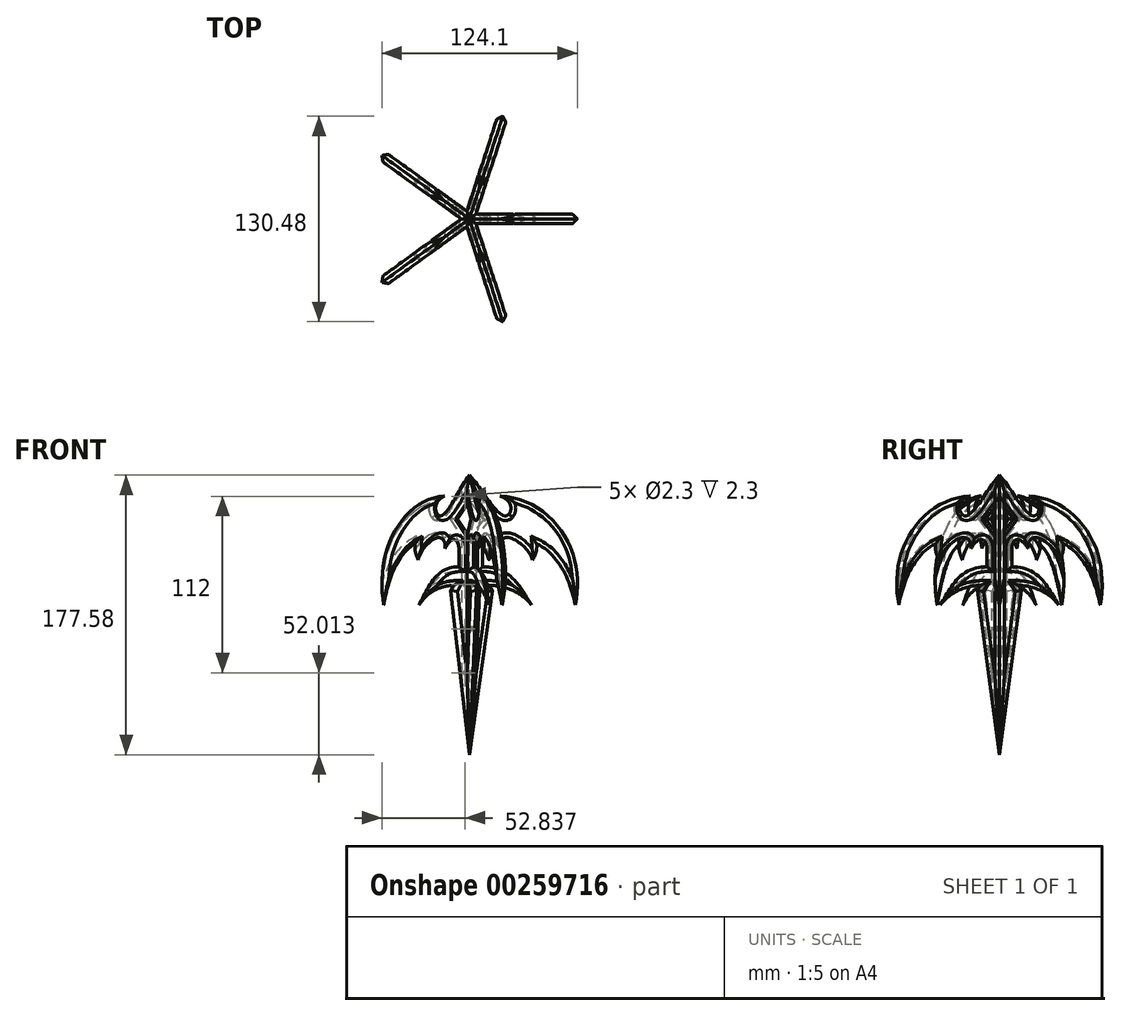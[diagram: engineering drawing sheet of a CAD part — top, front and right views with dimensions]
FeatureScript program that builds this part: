
annotation { "Feature Type Name" : "Feature", "Feature Type Description" : "" }
export const myFeature = defineFeature(function(context is Context, id is Id, definition is map)
    precondition{}
    {
        {
            var Q0;
            Q0=qCreatedBy(makeId("Front.planeOp"),FACE);
            cPlane(context, id + "F0", {"entities" : qUnion([Q0]), "cplaneType" : CPlaneType.OFFSET, "offset" : 3 * mm, "width" : 150 * mm, "height" : 150 * mm});
        }
        {
            var Q0;
            Q0=qCreatedBy(id+"F0.planeOp",FACE);
            var sketch = newSketch(context, id + "F1", { "sketchPlane" : qUnion([Q0])});
            skLineSegment(sketch, "E0", {"start": v(0, 75.85) * mm, "end": v(0, -61.56) * mm, "construction": true});
            skLineSegment(sketch, "E1.MirrorCS", {"start": v(0, 53.4) * mm, "end": v(9.24, 42.07) * mm});
            skLineSegment(sketch, "E2.MirrorCS", {"start": v(9.24, 42.07) * mm, "end": v(0, 30.82) * mm});
            skFitSpline(sketch, "E3.MirrorCS", {"points": [v(25.2, 45.18) * mm, v(0, 70) * mm], "startDerivative": vector(-18.57, -18.17) * mm, "endDerivative": vector(-25.2, 24.83) * mm});
            skFitSpline(sketch, "E4.MirrorCS", {"points": [v(67.26, -12.6) * mm, v(19.54, 56.74) * mm], "startDerivative": vector(23.53, 122.44) * mm, "endDerivative": vector(-82.56, 2.93) * mm});
            skFitSpline(sketch, "E5.MirrorCS", {"points": [v(67.26, -12.6) * mm, v(42.75, 26.42) * mm], "startDerivative": vector(-9.79, 47.9) * mm, "endDerivative": vector(-42.48, 20.2) * mm});
            skFitSpline(sketch, "E6.MirrorCS", {"points": [v(40.2, 16.18) * mm, v(19, 23.31) * mm], "startDerivative": vector(-5.4, 25.33) * mm, "endDerivative": vector(0, -47.43) * mm});
            skFitSpline(sketch, "E7.MirrorCS", {"points": [v(19, 23.31) * mm, v(8.27, 23.31) * mm], "startDerivative": vector(-14.05, 25.18) * mm, "endDerivative": vector(0, -20.5) * mm});
            skLineSegment(sketch, "E8.MirrorCS", {"start": v(8.27, 23.31) * mm, "end": v(8.27, 11.8) * mm});
            skFitSpline(sketch, "E9.MirrorCS", {"points": [v(8.27, 11.8) * mm, v(39.5, -12.6) * mm], "startDerivative": vector(52.7, 0) * mm, "endDerivative": vector(22.46, -37.8) * mm});
            skFitSpline(sketch, "E10.MirrorCS", {"points": [v(39.5, -12.6) * mm, v(12.57, 0) * mm], "startDerivative": vector(-19.32, 25.18) * mm, "endDerivative": vector(-29.86, 0) * mm});
            skLineSegment(sketch, "E11.MirrorCS", {"start": v(12.57, 0) * mm, "end": v(14.71, -3.23) * mm});
            skFitSpline(sketch, "E12.MirrorCS", {"points": [v(42.75, 26.42) * mm, v(40.2, 16.18) * mm], "startDerivative": vector(1.22, -12.7) * mm, "endDerivative": vector(-5.56, -9.14) * mm});
            skFitSpline(sketch, "E13.MirrorCS", {"points": [v(19.54, 56.74) * mm, v(25.2, 45.18) * mm], "startDerivative": vector(17.42, -5.07) * mm, "endDerivative": vector(-9.42, -13.46) * mm});
            skLineSegment(sketch, "E14", {"start": v(0, -107.57) * mm, "end": v(14.71, -3.23) * mm});
            skPoint(sketch, "E15.MirrorCS.start.orphan", {"position": v(14.71, -3.23) * mm});
            skLineSegment(sketch, "E16", {"start": v(0, 70) * mm, "end": v(0, 53.4) * mm});
            skLineSegment(sketch, "E17", {"start": v(0, 30.82) * mm, "end": v(0, -107.57) * mm});
            skSolve(sketch);
        }
        {
            var Q0;
            Q0 = qSketchRegion(id + "F1", true);
            extrude(context, id + "F2", {"entities" : qUnion([Q0]), "depth" : 6 * mm, "symmetric" : true});
        }
        {
            var Q0;
            Q0=makeQuery(id+"F2.opExtrude","CAP_EDGE",EDGE,{"disambiguationData":[OSD([sQuery(id+"F1.wireOp",EDGE,"E3.MirrorCS")])],"isStart":false});
            var Q1;
            Q1=makeQuery(id+"F2.opExtrude","CAP_EDGE",EDGE,{"disambiguationData":[OSD([sQuery(id+"F1.wireOp",EDGE,"E13.MirrorCS")])],"isStart":false});
            var Q2;
            Q2=makeQuery(id+"F2.opExtrude","CAP_EDGE",EDGE,{"disambiguationData":[OSD([sQuery(id+"F1.wireOp",EDGE,"E4.MirrorCS")])],"isStart":false});
            var Q3;
            Q3=makeQuery(id+"F2.opExtrude","CAP_EDGE",EDGE,{"disambiguationData":[OSD([sQuery(id+"F1.wireOp",EDGE,"E1.MirrorCS")])],"isStart":false});
            var Q4;
            Q4=makeQuery(id+"F2.opExtrude","CAP_EDGE",EDGE,{"disambiguationData":[OSD([sQuery(id+"F1.wireOp",EDGE,"E2.MirrorCS")])],"isStart":false});
            var Q5;
            Q5=makeQuery(id+"F2.opExtrude","CAP_EDGE",EDGE,{"disambiguationData":[OSD([sQuery(id+"F1.wireOp",EDGE,"E7.MirrorCS")])],"isStart":false});
            var Q6;
            Q6=makeQuery(id+"F2.opExtrude","CAP_EDGE",EDGE,{"disambiguationData":[OSD([sQuery(id+"F1.wireOp",EDGE,"E6.MirrorCS")])],"isStart":false});
            var Q7;
            Q7=makeQuery(id+"F2.opExtrude","CAP_EDGE",EDGE,{"disambiguationData":[OSD([sQuery(id+"F1.wireOp",EDGE,"E5.MirrorCS")])],"isStart":false});
            var Q8;
            Q8=makeQuery(id+"F2.opExtrude","CAP_EDGE",EDGE,{"disambiguationData":[OSD([sQuery(id+"F1.wireOp",EDGE,"E12.MirrorCS")])],"isStart":false});
            var Q9;
            Q9=makeQuery(id+"F2.opExtrude","CAP_EDGE",EDGE,{"disambiguationData":[OSD([sQuery(id+"F1.wireOp",EDGE,"E9.MirrorCS")])],"isStart":false});
            var Q10;
            Q10=makeQuery(id+"F2.opExtrude","CAP_EDGE",EDGE,{"disambiguationData":[OSD([sQuery(id+"F1.wireOp",EDGE,"E10.MirrorCS")])],"isStart":false});
            var Q11;
            Q11=makeQuery(id+"F2.opExtrude","CAP_EDGE",EDGE,{"disambiguationData":[OSD([sQuery(id+"F1.wireOp",EDGE,"E11.MirrorCS")])],"isStart":false});
            var Q12;
            Q12=makeQuery(id+"F2.opExtrude","CAP_EDGE",EDGE,{"disambiguationData":[OSD([sQuery(id+"F1.wireOp",EDGE,"E14")])],"isStart":false});
            var Q13;
            Q13=makeQuery(id+"F2.opExtrude","CAP_EDGE",EDGE,{"disambiguationData":[OSD([sQuery(id+"F1.wireOp",EDGE,"E3.MirrorCS")])],"isStart":true});
            var Q14;
            Q14=makeQuery(id+"F2.opExtrude","CAP_EDGE",EDGE,{"disambiguationData":[OSD([sQuery(id+"F1.wireOp",EDGE,"E13.MirrorCS")])],"isStart":true});
            var Q15;
            Q15=makeQuery(id+"F2.opExtrude","CAP_EDGE",EDGE,{"disambiguationData":[OSD([sQuery(id+"F1.wireOp",EDGE,"E4.MirrorCS")])],"isStart":true});
            var Q16;
            Q16=makeQuery(id+"F2.opExtrude","CAP_EDGE",EDGE,{"disambiguationData":[OSD([sQuery(id+"F1.wireOp",EDGE,"E1.MirrorCS")])],"isStart":true});
            var Q17;
            Q17=makeQuery(id+"F2.opExtrude","CAP_EDGE",EDGE,{"disambiguationData":[OSD([sQuery(id+"F1.wireOp",EDGE,"E2.MirrorCS")])],"isStart":true});
            var Q18;
            Q18=makeQuery(id+"F2.opExtrude","CAP_EDGE",EDGE,{"disambiguationData":[OSD([sQuery(id+"F1.wireOp",EDGE,"E7.MirrorCS")])],"isStart":true});
            var Q19;
            Q19=makeQuery(id+"F2.opExtrude","CAP_EDGE",EDGE,{"disambiguationData":[OSD([sQuery(id+"F1.wireOp",EDGE,"E6.MirrorCS")])],"isStart":true});
            var Q20;
            Q20=makeQuery(id+"F2.opExtrude","CAP_EDGE",EDGE,{"disambiguationData":[OSD([sQuery(id+"F1.wireOp",EDGE,"E5.MirrorCS")])],"isStart":true});
            var Q21;
            Q21=makeQuery(id+"F2.opExtrude","CAP_EDGE",EDGE,{"disambiguationData":[OSD([sQuery(id+"F1.wireOp",EDGE,"E12.MirrorCS")])],"isStart":true});
            var Q22;
            Q22=makeQuery(id+"F2.opExtrude","CAP_EDGE",EDGE,{"disambiguationData":[OSD([sQuery(id+"F1.wireOp",EDGE,"E9.MirrorCS")])],"isStart":true});
            var Q23;
            Q23=makeQuery(id+"F2.opExtrude","CAP_EDGE",EDGE,{"disambiguationData":[OSD([sQuery(id+"F1.wireOp",EDGE,"E10.MirrorCS")])],"isStart":true});
            var Q24;
            Q24=makeQuery(id+"F2.opExtrude","CAP_EDGE",EDGE,{"disambiguationData":[OSD([sQuery(id+"F1.wireOp",EDGE,"E11.MirrorCS")])],"isStart":true});
            var Q25;
            Q25=makeQuery(id+"F2.opExtrude","CAP_EDGE",EDGE,{"disambiguationData":[OSD([sQuery(id+"F1.wireOp",EDGE,"E14")])],"isStart":true});
            chamfer(context, id + "F3", {"entities" : qUnion([Q0, Q1, Q2, Q3, Q4, Q5, Q6, Q7, Q8, Q9, Q10, Q11, Q12, Q13, Q14, Q15, Q16, Q17, Q18, Q19, Q20, Q21, Q22, Q23, Q24, Q25]), "width" : 3 * mm, "tangentPropagation" : true});
        }
        {
            var Q0;
            Q0=qCreatedBy(makeId("Front.planeOp"),FACE);
            cPlane(context, id + "F4", {"entities" : qUnion([Q0]), "cplaneType" : CPlaneType.OFFSET, "offset" : 3 * mm, "width" : 150 * mm, "height" : 150 * mm});
        }
        {
            var Q0;
            Q0=qCreatedBy(id+"F4.planeOp",FACE);
            var sketch = newSketch(context, id + "F5", { "sketchPlane" : qUnion([Q0])});
            skLineSegment(sketch, "E18", {"start": v(0, 74.1) * mm, "end": v(0, -133.44) * mm, "construction": true});
            skSolve(sketch);
        }
        {
            var Q0;
            Q0=qCreatedBy(makeId("Top.planeOp"),FACE);
            var sketch = newSketch(context, id + "F6", { "sketchPlane" : qUnion([Q0])});
            skLineSegment(sketch, "E19", {"start": v(0, -3) * mm, "end": v(74.44, -3) * mm, "construction": true});
            skLineSegment(sketch, "E20", {"start": v(0, -3) * mm, "end": v(6.88, -8) * mm});
            skLineSegment(sketch, "E21", {"start": v(6.88, -8) * mm, "end": v(0, -8) * mm});
            skLineSegment(sketch, "E22", {"start": v(0, -8) * mm, "end": v(0, -3) * mm});
            skLineSegment(sketch, "E23.MirrorCS", {"start": v(0, 2) * mm, "end": v(0, -3) * mm});
            skLineSegment(sketch, "E24.MirrorCS", {"start": v(0, -3) * mm, "end": v(6.88, 2) * mm});
            skLineSegment(sketch, "E25.MirrorCS", {"start": v(6.88, 2) * mm, "end": v(0, 2) * mm});
            skSolve(sketch);
        }
        {
            var Q0;
            Q0 = qSketchRegion(id + "F6", true);
            extrude(context, id + "F7", {"entities" : qUnion([Q0]), "operationType" : NewBodyOperationType.REMOVE, "oppositeDirection" : true, "depth" : 300 * mm, "symmetric" : true});
        }
        {
            var Q0;
            {var subQ1=sQuery(id+"F1.wireOp",EDGE,"E2.MirrorCS");Q0=makeQuery(id+"F7.boolean.opBoolean","COPY",FACE,{"disambiguationData":[TD([makeQuery(id+"F3.opChamfer","BLEND_FACE",FACE,{"disambiguationData":[OSD([subQ1]),TDD([makeQuery(id+"F2.opExtrude","CAP_EDGE",EDGE,{"disambiguationData":[OSD([subQ1])],"isStart":true})])]})])],"derivedFrom":makeQuery(id+"F7.opExtrude","SWEPT_FACE",FACE,{"disambiguationData":[OSD([sQuery(id+"F6.wireOp",EDGE,"E20")])]})});}
            var sketch = newSketch(context, id + "F8", { "sketchPlane" : qUnion([Q0])});
            skLineSegment(sketch, "E26", {"start": v(6.87, 74.88) * mm, "end": v(6.87, -85.39) * mm, "construction": true});
            skLineSegment(sketch, "E27", {"start": v(1.76, 75.39) * mm, "end": v(1.76, -86.65) * mm, "construction": true});
            skLineSegment(sketch, "E28", {"start": v(4.32, 67.98) * mm, "end": v(4.32, -97.89) * mm, "construction": true});
            skPoint(sketch, "E28.startSnap0", {"position": v(4.32, 30.97) * mm});
            skPoint(sketch, "E28.endSnap0", {"position": v(4.32, -82.19) * mm});
            skCircle(sketch, "E29", {"center": v(4.32, 56.43) * mm, "radius": 1 * mm});
            skCircle(sketch, "E30.0.1.0", {"center": v(4.32, 28.43) * mm, "radius": 1 * mm});
            skCircle(sketch, "E30.0.2.0", {"center": v(4.32, 0.43) * mm, "radius": 1 * mm});
            skCircle(sketch, "E30.0.3.0", {"center": v(4.32, -27.57) * mm, "radius": 1 * mm});
            skCircle(sketch, "E30.0.4.0", {"center": v(4.32, -55.57) * mm, "radius": 1 * mm});
            skLineSegment(sketch, "E30.direction1", {"start": v(4.32, 56.43) * mm, "end": v(29.32, 56.43) * mm, "construction": true});
            skLineSegment(sketch, "E30.direction2", {"start": v(4.32, 56.43) * mm, "end": v(4.32, 28.43) * mm, "construction": true});
            skSolve(sketch);
        }
        {
            var Q0;
            Q0 = qSketchRegion(id + "F8", true);
            extrude(context, id + "F9", {"entities" : qUnion([Q0]), "operationType" : NewBodyOperationType.ADD, "depth" : 2 * mm});
        }
        {
            var Q0;
            {var subQ0=sQuery(id+"F1.wireOp",EDGE,"E2.MirrorCS");Q0=makeQuery(id+"F7.boolean.opBoolean","COPY",FACE,{"disambiguationData":[TD([makeQuery(id+"F3.opChamfer","BLEND_FACE",FACE,{"disambiguationData":[OSD([subQ0]),TDD([makeQuery(id+"F2.opExtrude","CAP_EDGE",EDGE,{"disambiguationData":[OSD([subQ0])],"isStart":true})])]})])],"derivedFrom":makeQuery(id+"F7.opExtrude","SWEPT_FACE",FACE,{"disambiguationData":[OSD([sQuery(id+"F6.wireOp",EDGE,"E24.MirrorCS")])]})});}
            var sketch = newSketch(context, id + "F10", { "sketchPlane" : qUnion([Q0])});
            skLineSegment(sketch, "E31", {"start": v(1.65, 74.9) * mm, "end": v(1.65, -85.37) * mm, "construction": true});
            skLineSegment(sketch, "E32", {"start": v(-3.45, 75.4) * mm, "end": v(-3.45, -86.63) * mm, "construction": true});
            skLineSegment(sketch, "E33", {"start": v(-0.9, 68) * mm, "end": v(-0.9, -97.87) * mm, "construction": true});
            skPoint(sketch, "E33.startSnap0", {"position": v(-0.9, 30.99) * mm});
            skPoint(sketch, "E33.endSnap0", {"position": v(-0.9, -82.17) * mm});
            skCircle(sketch, "E34", {"center": v(-0.9, 56.44) * mm, "radius": 1.15 * mm});
            skCircle(sketch, "E35.0.1.0", {"center": v(-0.9, 28.44) * mm, "radius": 1.15 * mm});
            skCircle(sketch, "E35.0.2.0", {"center": v(-0.9, 0.44) * mm, "radius": 1.15 * mm});
            skCircle(sketch, "E35.0.3.0", {"center": v(-0.9, -27.56) * mm, "radius": 1.15 * mm});
            skCircle(sketch, "E35.0.4.0", {"center": v(-0.9, -55.56) * mm, "radius": 1.15 * mm});
            skLineSegment(sketch, "E35.direction1", {"start": v(-0.9, 56.44) * mm, "end": v(24.1, 56.44) * mm, "construction": true});
            skLineSegment(sketch, "E35.direction2", {"start": v(-0.9, 56.44) * mm, "end": v(-0.9, 28.44) * mm, "construction": true});
            skSolve(sketch);
        }
        {
            var Q0;
            Q0 = qSketchRegion(id + "F10", true);
            extrude(context, id + "F11", {"entities" : qUnion([Q0]), "operationType" : NewBodyOperationType.REMOVE, "oppositeDirection" : true, "depth" : 2.3 * mm});
        }
        {
            var Q0;
            Q0=makeQuery(id+"F2.opExtrude","SWEPT_BODY",BODY,{"disambiguationData":[OSD([sQuery(id+"F1.wireOp",EDGE,"E1.MirrorCS"),sQuery(id+"F1.wireOp",EDGE,"E2.MirrorCS"),sQuery(id+"F1.wireOp",EDGE,"E3.MirrorCS"),sQuery(id+"F1.wireOp",EDGE,"E4.MirrorCS"),sQuery(id+"F1.wireOp",EDGE,"E5.MirrorCS"),sQuery(id+"F1.wireOp",EDGE,"E6.MirrorCS"),sQuery(id+"F1.wireOp",EDGE,"E7.MirrorCS"),sQuery(id+"F1.wireOp",EDGE,"E8.MirrorCS"),sQuery(id+"F1.wireOp",EDGE,"E9.MirrorCS"),sQuery(id+"F1.wireOp",EDGE,"E10.MirrorCS"),sQuery(id+"F1.wireOp",EDGE,"E11.MirrorCS"),sQuery(id+"F1.wireOp",EDGE,"E12.MirrorCS"),sQuery(id+"F1.wireOp",EDGE,"E13.MirrorCS"),sQuery(id+"F1.wireOp",EDGE,"E14"),sQuery(id+"F1.wireOp",EDGE,"E16"),sQuery(id+"F1.wireOp",EDGE,"E17")])]});
            var Q1;
            Q1=sQuery(id+"F5.wireOp",EDGE,"E18");
            circularPattern(context, id + "F12", {"entities" : qUnion([Q0]), "axis" : qUnion([Q1]), "angle" : 360 * degree, "instanceCount" : 5, "equalSpace" : true, "computeTransformsWithoutBuiltin" : true});
        }
    });
